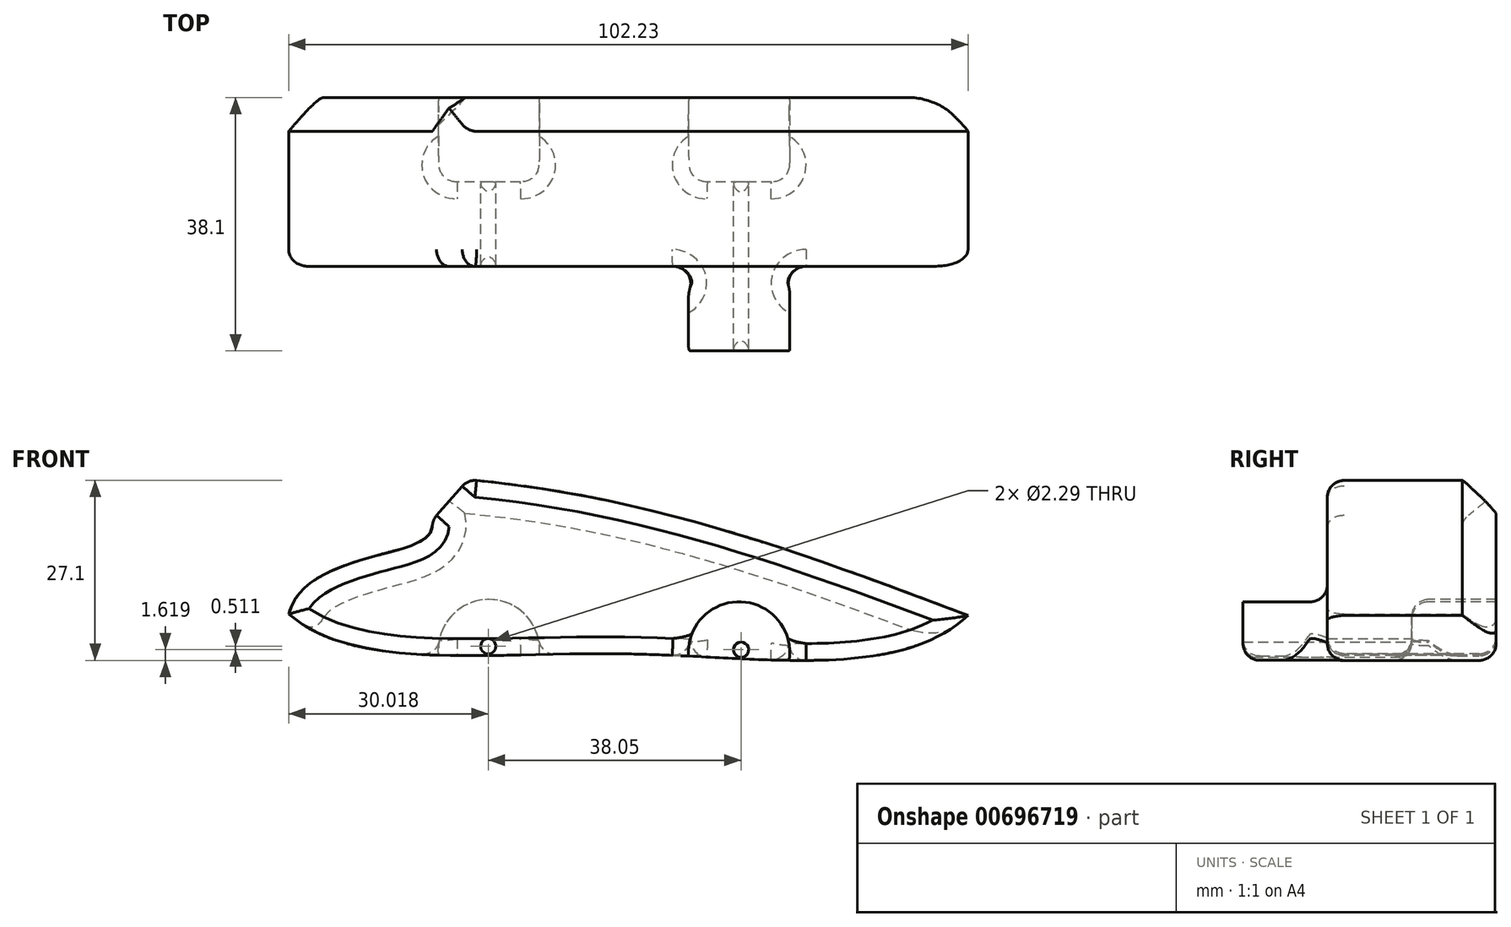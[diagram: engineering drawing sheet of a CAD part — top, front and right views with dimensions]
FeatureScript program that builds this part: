
annotation { "Feature Type Name" : "Feature", "Feature Type Description" : "" }
export const myFeature = defineFeature(function(context is Context, id is Id, definition is map)
    precondition{}
    {
        {
            var Q0;
            Q0=qCreatedBy(makeId("Front.planeOp"),FACE);
            var sketch = newSketch(context, id + "F0", { "sketchPlane" : qUnion([Q0])});
            skPoint(sketch, "E0", {"position": v(-50.8, 25.4) * mm});
            skPoint(sketch, "E1", {"position": v(50.8, -25.4) * mm});
            skFitSpline(sketch, "E2", {"points": [v(51.43, -0.2) * mm, v(0, 16.49) * mm, v(-58.25, 20.67) * mm], "startDerivative": vector(-99.9, 37.94) * mm, "endDerivative": vector(-127.36, -7.27) * mm});
            skFitSpline(sketch, "E3", {"points": [v(-36.61, 21.9) * mm, v(-36.61, 9.08) * mm, v(-50.8, 0) * mm], "startDerivative": vector(84.34, -62.8) * mm, "endDerivative": vector(-7.01, -28.72) * mm});
            skLineSegment(sketch, "E4", {"start": v(-50.8, 0) * mm, "end": v(51.43, -0.2) * mm});
            skFitSpline(sketch, "E5", {"points": [v(-50.8, 0) * mm, v(0, -5.97) * mm, v(51.43, -0.2) * mm], "startDerivative": vector(60.04, -52.53) * mm, "endDerivative": vector(64.63, 59.22) * mm});
            skSolve(sketch);
        }
        {
            var Q0;
            Q0 = qSketchRegion(id + "F0", true);
            extrude(context, id + "F1", {"entities" : qUnion([Q0]), "endBound" : BoundingType.SYMMETRIC, "depth" : 38.1 * mm, "offsetDistance" : 25.4 * mm});
        }
        {
            var Q0;
            Q0=makeQuery(id+"F1.opExtrude","SWEPT_EDGE",EDGE,{"disambiguationData":[OSD([sQuery(id+"F0.wireOp",EDGE,"E2"),sQuery(id+"F0.wireOp",EDGE,"E3")])]});
            chamfer(context, id + "F2", {"entities" : qUnion([Q0]), "width" : 5.08 * mm, "tangentPropagation" : true});
        }
        {
            var Q0;
            Q0=makeQuery(id+"F1.opExtrude","CAP_FACE",FACE,{"disambiguationData":[OSD([sQuery(id+"F0.wireOp",EDGE,"E2"),sQuery(id+"F0.wireOp",EDGE,"E3"),sQuery(id+"F0.wireOp",EDGE,"E5")])],"isStart":false});
            var sketch = newSketch(context, id + "F3", { "sketchPlane" : qUnion([Q0])});
            skCircle(sketch, "E6", {"center": v(-20.67, -5.4) * mm, "radius": 7.62 * mm});
            skCircle(sketch, "E7.MirrorC", {"center": v(16.97, -5.75) * mm, "radius": 7.62 * mm});
            skSolve(sketch);
        }
        {
            var Q0;
            {var subQ0=sQuery(id+"F3.wireOp",EDGE,"E6");var subQ1=sQuery(id+"F0.wireOp",EDGE,"E5");var subQ2=makeQuery(id+"FuxhyJIyCqlSASX_1.opFillet","BLEND_EDGE",EDGE,{"blendedFrom":[makeQuery(id+"F1.opExtrude","CAP_EDGE",EDGE,{"disambiguationData":[OSD([subQ1])],"isStart":false}),makeQuery(id+"F1.opExtrude","CAP_FACE",FACE,{"disambiguationData":[OSD([sQuery(id+"F0.wireOp",EDGE,"E2"),sQuery(id+"F0.wireOp",EDGE,"E3"),subQ1])],"isStart":false})],"blendedInto":[makeQuery(id+"F1.opExtrude","CAP_FACE",FACE,{"disambiguationData":[OSD([sQuery(id+"F0.wireOp",EDGE,"E2"),sQuery(id+"F0.wireOp",EDGE,"E3"),subQ1])],"isStart":false})]});var subQ3=makeQuery(id+"F3.imprint","INTERSECT",VERTEX,{"disambiguationData":[OD(0.0)],"derivedFrom":[subQ2,subQ0]});Q0=makeQuery(id+"F3.imprint","IMPRINT",FACE,{"disambiguationData":[TD([[makeQuery(id+"F3.imprint","IMPRINT",EDGE,{"disambiguationData":[TD([[subQ3,-1.0]])],"derivedFrom":subQ0}),1.0]])]});}
            var Q1;
            {var subQ0=sQuery(id+"F3.wireOp",EDGE,"E6");var subQ1=sQuery(id+"F0.wireOp",EDGE,"E5");var subQ2=makeQuery(id+"FuxhyJIyCqlSASX_1.opFillet","BLEND_EDGE",EDGE,{"blendedFrom":[makeQuery(id+"F1.opExtrude","CAP_EDGE",EDGE,{"disambiguationData":[OSD([subQ1])],"isStart":false}),makeQuery(id+"F1.opExtrude","CAP_FACE",FACE,{"disambiguationData":[OSD([sQuery(id+"F0.wireOp",EDGE,"E2"),sQuery(id+"F0.wireOp",EDGE,"E3"),subQ1])],"isStart":false})],"blendedInto":[makeQuery(id+"F1.opExtrude","CAP_FACE",FACE,{"disambiguationData":[OSD([sQuery(id+"F0.wireOp",EDGE,"E2"),sQuery(id+"F0.wireOp",EDGE,"E3"),subQ1])],"isStart":false})]});var subQ3=makeQuery(id+"F3.imprint","INTERSECT",VERTEX,{"disambiguationData":[OD(0.0)],"derivedFrom":[subQ2,subQ0]});Q1=makeQuery(id+"F3.imprint","IMPRINT",FACE,{"disambiguationData":[TD([[makeQuery(id+"F3.imprint","IMPRINT",EDGE,{"disambiguationData":[TD([[subQ3,1.0]])],"derivedFrom":subQ0}),1.0]])]});}
            var Q2;
            {var subQ0=sQuery(id+"F3.wireOp",EDGE,"E7.MirrorC");var subQ1=sQuery(id+"F0.wireOp",EDGE,"E5");var subQ2=makeQuery(id+"FuxhyJIyCqlSASX_1.opFillet","BLEND_EDGE",EDGE,{"blendedFrom":[makeQuery(id+"F1.opExtrude","CAP_EDGE",EDGE,{"disambiguationData":[OSD([subQ1])],"isStart":false}),makeQuery(id+"F1.opExtrude","CAP_FACE",FACE,{"disambiguationData":[OSD([sQuery(id+"F0.wireOp",EDGE,"E2"),sQuery(id+"F0.wireOp",EDGE,"E3"),subQ1])],"isStart":false})],"blendedInto":[makeQuery(id+"F1.opExtrude","CAP_FACE",FACE,{"disambiguationData":[OSD([sQuery(id+"F0.wireOp",EDGE,"E2"),sQuery(id+"F0.wireOp",EDGE,"E3"),subQ1])],"isStart":false})]});var subQ3=makeQuery(id+"F3.imprint","INTERSECT",VERTEX,{"disambiguationData":[OD(0.0)],"derivedFrom":[subQ2,subQ0]});Q2=makeQuery(id+"F3.imprint","IMPRINT",FACE,{"disambiguationData":[TD([[makeQuery(id+"F3.imprint","IMPRINT",EDGE,{"disambiguationData":[TD([[subQ3,-1.0]])],"derivedFrom":subQ0}),-1.0]])]});}
            var Q3;
            {var subQ0=sQuery(id+"F3.wireOp",EDGE,"E7.MirrorC");var subQ1=sQuery(id+"F0.wireOp",EDGE,"E5");var subQ2=makeQuery(id+"FuxhyJIyCqlSASX_1.opFillet","BLEND_EDGE",EDGE,{"blendedFrom":[makeQuery(id+"F1.opExtrude","CAP_EDGE",EDGE,{"disambiguationData":[OSD([subQ1])],"isStart":false}),makeQuery(id+"F1.opExtrude","CAP_FACE",FACE,{"disambiguationData":[OSD([sQuery(id+"F0.wireOp",EDGE,"E2"),sQuery(id+"F0.wireOp",EDGE,"E3"),subQ1])],"isStart":false})],"blendedInto":[makeQuery(id+"F1.opExtrude","CAP_FACE",FACE,{"disambiguationData":[OSD([sQuery(id+"F0.wireOp",EDGE,"E2"),sQuery(id+"F0.wireOp",EDGE,"E3"),subQ1])],"isStart":false})]});var subQ3=makeQuery(id+"F3.imprint","INTERSECT",VERTEX,{"disambiguationData":[OD(0.0)],"derivedFrom":[subQ2,subQ0]});Q3=makeQuery(id+"F3.imprint","IMPRINT",FACE,{"disambiguationData":[TD([[makeQuery(id+"F3.imprint","IMPRINT",EDGE,{"disambiguationData":[TD([[subQ3,1.0]])],"derivedFrom":subQ0}),-1.0]])]});}
            extrude(context, id + "F4", {"entities" : qUnion([Q0, Q1, Q2, Q3]), "operationType" : NewBodyOperationType.REMOVE, "endBound" : BoundingType.SYMMETRIC, "depth" : 25.4 * mm, "offsetDistance" : 25.4 * mm});
        }
        {
            var Q0;
            Q0=makeQuery(id+"F1.opExtrude","CAP_EDGE",EDGE,{"disambiguationData":[OSD([sQuery(id+"F0.wireOp",EDGE,"E2")])],"isStart":false});
            var Q1;
            Q1=makeQuery(id+"F1.opExtrude","CAP_EDGE",EDGE,{"disambiguationData":[OSD([sQuery(id+"F0.wireOp",EDGE,"E2")])],"isStart":true});
            var Q2;
            Q2=makeQuery(id+"F1.opExtrude","CAP_EDGE",EDGE,{"disambiguationData":[OSD([sQuery(id+"F0.wireOp",EDGE,"E3")])],"isStart":false});
            var Q3;
            Q3=makeQuery(id+"F1.opExtrude","CAP_EDGE",EDGE,{"disambiguationData":[OSD([sQuery(id+"F0.wireOp",EDGE,"E3")])],"isStart":true});
            chamfer(context, id + "F5", {"entities" : qUnion([Q0, Q1, Q2, Q3]), "width" : 5.08 * mm, "tangentPropagation" : true});
        }
        {
            var Q0;
            Q0=makeQuery(id+"F4.boolean.opBoolean","COPY",FACE,{"derivedFrom":makeQuery(id+"F4.opExtrude","CAP_FACE",FACE,{"disambiguationData":[OSD([sQuery(id+"F3.wireOp",EDGE,"E6")])],"isStart":true})});
            var Q1;
            Q1=makeQuery(id+"F4.boolean.opBoolean","COPY",FACE,{"derivedFrom":makeQuery(id+"F4.opExtrude","CAP_FACE",FACE,{"disambiguationData":[OSD([sQuery(id+"F3.wireOp",EDGE,"E7.MirrorC")])],"isStart":true})});
            fillet(context, id + "F6", {"entities" : qUnion([Q0, Q1]), "radius" : 2.54 * mm, "tangentPropagation" : true, "allowEdgeOverflow" : false});
        }
        {
            var Q0;
            {var subQ0=sQuery(id+"F0.wireOp",EDGE,"E2");Q0=makeQuery(id+"F2.opChamfer","BLEND_EDGE",EDGE,{"blendedFrom":[makeQuery(id+"F1.opExtrude","SWEPT_EDGE",EDGE,{"disambiguationData":[OSD([subQ0,sQuery(id+"F0.wireOp",EDGE,"E3")])]}),makeQuery(id+"F1.opExtrude","SWEPT_FACE",FACE,{"disambiguationData":[OSD([subQ0])]})],"blendedInto":[makeQuery(id+"F1.opExtrude","SWEPT_FACE",FACE,{"disambiguationData":[OSD([subQ0])]})]});}
            var Q1;
            {var subQ0=sQuery(id+"F0.wireOp",EDGE,"E3");Q1=makeQuery(id+"F2.opChamfer","BLEND_EDGE",EDGE,{"blendedFrom":[makeQuery(id+"F1.opExtrude","SWEPT_EDGE",EDGE,{"disambiguationData":[OSD([sQuery(id+"F0.wireOp",EDGE,"E2"),subQ0])]}),makeQuery(id+"F1.opExtrude","SWEPT_FACE",FACE,{"disambiguationData":[OSD([subQ0])]})],"blendedInto":[makeQuery(id+"F1.opExtrude","SWEPT_FACE",FACE,{"disambiguationData":[OSD([subQ0])]})]});}
            fillet(context, id + "F7", {"entities" : qUnion([Q0, Q1]), "radius" : 2.54 * mm, "tangentPropagation" : true, "allowEdgeOverflow" : false});
        }
        {
            var Q0;
            {var subQ0=sQuery(id+"F0.wireOp",EDGE,"E5");var subQ1=sQuery(id+"F0.wireOp",EDGE,"E3");Q0=makeQuery(id+"F4.boolean.opBoolean","SPLIT",EDGE,{"disambiguationData":[TD([makeQuery(id+"F1.opExtrude","CAP_FACE",FACE,{"disambiguationData":[OSD([sQuery(id+"F0.wireOp",EDGE,"E2"),subQ1,subQ0])],"isStart":false}),makeQuery(id+"F1.opExtrude","SWEPT_FACE",FACE,{"disambiguationData":[OSD([subQ1])]}),makeQuery(id+"F1.opExtrude","SWEPT_FACE",FACE,{"disambiguationData":[OSD([subQ0])]}),makeQuery(id+"F4.opExtrude","SWEPT_FACE",FACE,{"disambiguationData":[OSD([sQuery(id+"F3.wireOp",EDGE,"E6")])]})])],"derivedFrom":makeQuery(id+"F1.opExtrude","CAP_EDGE",EDGE,{"disambiguationData":[OSD([subQ0])],"isStart":false})});}
            var Q1;
            Q1=makeQuery(id+"F1.opExtrude","CAP_EDGE",EDGE,{"disambiguationData":[OSD([sQuery(id+"F0.wireOp",EDGE,"E5")])],"isStart":true});
            fillet(context, id + "F8", {"entities" : qUnion([Q0, Q1]), "radius" : 2.54 * mm, "tangentPropagation" : true, "allowEdgeOverflow" : false});
        }
        {
            var Q0;
            Q0=makeQuery(id+"F1.opExtrude","CAP_FACE",FACE,{"disambiguationData":[OSD([sQuery(id+"F0.wireOp",EDGE,"E2"),sQuery(id+"F0.wireOp",EDGE,"E3"),sQuery(id+"F0.wireOp",EDGE,"E5")])],"isStart":true});
            var sketch = newSketch(context, id + "F9", { "sketchPlane" : qUnion([Q0])});
            skLineSegment(sketch, "E8", {"start": v(20.67, -5.4) * mm, "end": v(-16.97, -5.75) * mm, "construction": true});
            skCircle(sketch, "E9", {"center": v(20.67, -5.4) * mm, "radius": 7.62 * mm});
            skCircle(sketch, "E10", {"center": v(-16.97, -5.75) * mm, "radius": 7.62 * mm});
            skSolve(sketch);
        }
        {
            var Q0;
            {var subQ0=sQuery(id+"F9.wireOp",EDGE,"E10");var subQ1=makeQuery(id+"F1.opExtrude","CAP_EDGE",EDGE,{"disambiguationData":[OSD([sQuery(id+"F0.wireOp",EDGE,"E5")])],"isStart":true});var subQ2=makeQuery(id+"F9.imprint","INTERSECT",VERTEX,{"disambiguationData":[OD(0.0)],"derivedFrom":[subQ1,subQ0]});Q0=makeQuery(id+"F9.imprint","IMPRINT",FACE,{"disambiguationData":[TD([[makeQuery(id+"F9.imprint","IMPRINT",EDGE,{"disambiguationData":[TD([[subQ2,-1.0]])],"derivedFrom":subQ0}),1.0]])]});}
            var Q1;
            {var subQ0=sQuery(id+"F9.wireOp",EDGE,"E10");var subQ1=makeQuery(id+"F1.opExtrude","CAP_EDGE",EDGE,{"disambiguationData":[OSD([sQuery(id+"F0.wireOp",EDGE,"E5")])],"isStart":true});var subQ2=makeQuery(id+"F9.imprint","INTERSECT",VERTEX,{"disambiguationData":[OD(0.0)],"derivedFrom":[subQ1,subQ0]});Q1=makeQuery(id+"F9.imprint","IMPRINT",FACE,{"disambiguationData":[TD([[makeQuery(id+"F9.imprint","IMPRINT",EDGE,{"disambiguationData":[TD([[subQ2,1.0]])],"derivedFrom":subQ0}),1.0]])]});}
            var Q2;
            {var subQ0=sQuery(id+"F9.wireOp",EDGE,"E9");var subQ1=makeQuery(id+"F1.opExtrude","CAP_EDGE",EDGE,{"disambiguationData":[OSD([sQuery(id+"F0.wireOp",EDGE,"E5")])],"isStart":true});var subQ2=makeQuery(id+"F9.imprint","INTERSECT",VERTEX,{"disambiguationData":[OD(0.0)],"derivedFrom":[subQ1,subQ0]});Q2=makeQuery(id+"F9.imprint","IMPRINT",FACE,{"disambiguationData":[TD([[makeQuery(id+"F9.imprint","IMPRINT",EDGE,{"disambiguationData":[TD([[subQ2,1.0]])],"derivedFrom":subQ0}),1.0]])]});}
            var Q3;
            {var subQ0=sQuery(id+"F9.wireOp",EDGE,"E9");var subQ1=makeQuery(id+"F1.opExtrude","CAP_EDGE",EDGE,{"disambiguationData":[OSD([sQuery(id+"F0.wireOp",EDGE,"E5")])],"isStart":true});var subQ2=makeQuery(id+"F9.imprint","INTERSECT",VERTEX,{"disambiguationData":[OD(0.0)],"derivedFrom":[subQ1,subQ0]});Q3=makeQuery(id+"F9.imprint","IMPRINT",FACE,{"disambiguationData":[TD([[makeQuery(id+"F9.imprint","IMPRINT",EDGE,{"disambiguationData":[TD([[subQ2,-1.0]])],"derivedFrom":subQ0}),1.0]])]});}
            extrude(context, id + "F10", {"entities" : qUnion([Q0, Q1, Q2, Q3]), "operationType" : NewBodyOperationType.REMOVE, "endBound" : BoundingType.SYMMETRIC, "depth" : 25.4 * mm, "offsetDistance" : 25.4 * mm});
        }
        {
            var Q0;
            Q0=makeQuery(id+"F10.boolean.opBoolean","COPY",FACE,{"derivedFrom":makeQuery(id+"F10.opExtrude","CAP_FACE",FACE,{"disambiguationData":[OSD([sQuery(id+"F9.wireOp",EDGE,"E10")])],"isStart":true})});
            var Q1;
            Q1=makeQuery(id+"F10.boolean.opBoolean","COPY",FACE,{"derivedFrom":makeQuery(id+"F10.opExtrude","CAP_FACE",FACE,{"disambiguationData":[OSD([sQuery(id+"F9.wireOp",EDGE,"E9")])],"isStart":true})});
            fillet(context, id + "F11", {"entities" : qUnion([Q0, Q1]), "radius" : 2.54 * mm, "tangentPropagation" : true, "allowEdgeOverflow" : false});
        }
        {
            var Q0;
            Q0=qCreatedBy(makeId("Front.planeOp"),FACE);
            var sketch = newSketch(context, id + "F12", { "sketchPlane" : qUnion([Q0])});
            skCircle(sketch, "E11", {"center": v(17.27, -5.34) * mm, "radius": 1.14 * mm});
            skSolve(sketch);
        }
        {
            var Q0;
            Q0 = qSketchRegion(id + "F12", true);
            extrude(context, id + "F13", {"entities" : qUnion([Q0]), "operationType" : NewBodyOperationType.REMOVE, "endBound" : BoundingType.SYMMETRIC, "depth" : 50.8 * mm, "offsetDistance" : 25.4 * mm});
        }
        {
            var Q0;
            Q0=qCreatedBy(makeId("Front.planeOp"),FACE);
            var sketch = newSketch(context, id + "F14", { "sketchPlane" : qUnion([Q0])});
            skCircle(sketch, "E12", {"center": v(-20.78, -4.83) * mm, "radius": 1.14 * mm});
            skSolve(sketch);
        }
        {
            var Q0;
            Q0=makeQuery(id+"F14.imprint","IMPRINT",FACE,{"disambiguationData":[TD([[makeQuery(id+"F14.imprint","IMPRINT",EDGE,{"derivedFrom":sQuery(id+"F14.wireOp",EDGE,"E12")}),1.0]])]});
            extrude(context, id + "F15", {"entities" : qUnion([Q0]), "operationType" : NewBodyOperationType.REMOVE, "endBound" : BoundingType.SYMMETRIC, "depth" : 50.8 * mm, "offsetDistance" : 25.4 * mm});
        }
    });
